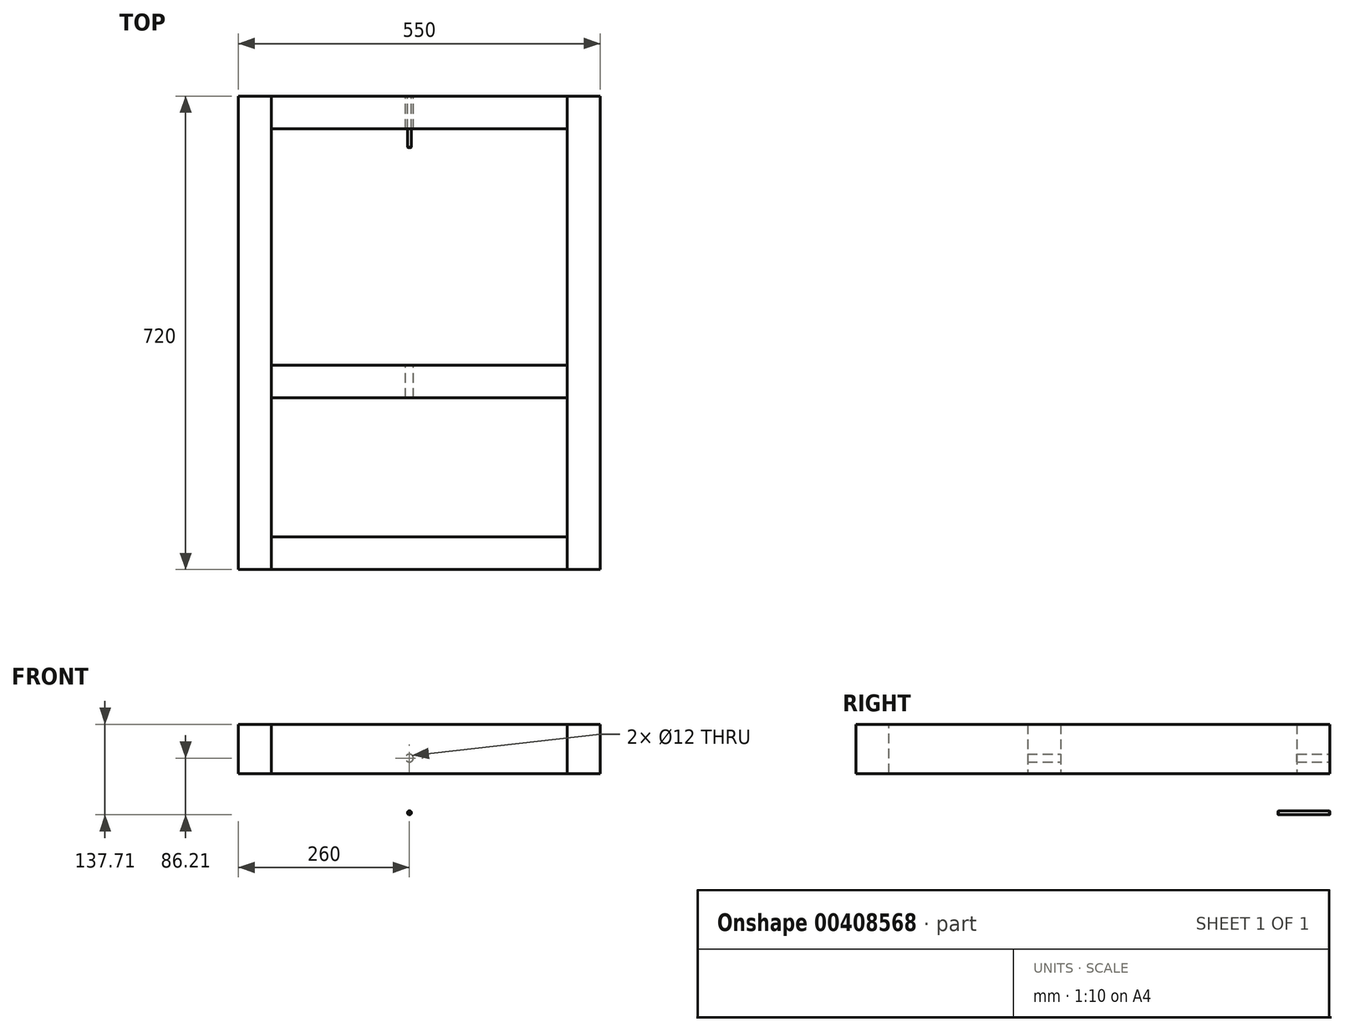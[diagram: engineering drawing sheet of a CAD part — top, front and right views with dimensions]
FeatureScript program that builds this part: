
annotation { "Feature Type Name" : "Feature", "Feature Type Description" : "" }
export const myFeature = defineFeature(function(context is Context, id is Id, definition is map)
    precondition{}
    {
        {
            var Q0;
            Q0=qCreatedBy(makeId("Front.planeOp"),FACE);
            var sketch = newSketch(context, id + "F0", { "sketchPlane" : qUnion([Q0])});
            skLineSegment(sketch, "E0.bottom", {"start": v(225, 37.5) * mm, "end": v(-225, 37.5) * mm});
            skLineSegment(sketch, "E0.top", {"start": v(225, -37.5) * mm, "end": v(-225, -37.5) * mm});
            skLineSegment(sketch, "E0.left", {"start": v(225, 37.5) * mm, "end": v(225, -37.5) * mm});
            skLineSegment(sketch, "E0.right", {"start": v(-225, 37.5) * mm, "end": v(-225, -37.5) * mm});
            skPoint(sketch, "E0.middle", {"position": v(0, 0) * mm});
            skLineSegment(sketch, "E1.bottom", {"start": v(225, 37.5) * mm, "end": v(275, 37.5) * mm});
            skLineSegment(sketch, "E1.top", {"start": v(225, -37.5) * mm, "end": v(275, -37.5) * mm});
            skLineSegment(sketch, "E1.right", {"start": v(275, 37.5) * mm, "end": v(275, -37.5) * mm});
            skLineSegment(sketch, "E2.bottom", {"start": v(-225, 37.5) * mm, "end": v(-275, 37.5) * mm});
            skLineSegment(sketch, "E2.top", {"start": v(-225, -37.5) * mm, "end": v(-275, -37.5) * mm});
            skLineSegment(sketch, "E2.right", {"start": v(-275, 37.5) * mm, "end": v(-275, -37.5) * mm});
            skLineSegment(sketch, "E3", {"start": v(225, -14) * mm, "end": v(-225, -14) * mm, "construction": true});
            skLineSegment(sketch, "E4", {"start": v(-15, 37.5) * mm, "end": v(-15, -37.5) * mm, "construction": true});
            skCircle(sketch, "E5", {"center": v(-15, -14) * mm, "radius": 6 * mm});
            skCircle(sketch, "E6", {"center": v(-15, -97.21) * mm, "radius": 3 * mm});
            skSolve(sketch);
        }
        {
            var Q0;
            Q0=makeQuery(id+"F0.imprint","IMPRINT",FACE,{"disambiguationData":[TD([[makeQuery(id+"F0.imprint","IMPRINT",EDGE,{"derivedFrom":sQuery(id+"F0.wireOp",EDGE,"E0.bottom")}),1.0]])]});
            extrude(context, id + "F1", {"entities" : qUnion([Q0]), "depth" : 50 * mm});
        }
        {
            var Q0;
            Q0=makeQuery(id+"F0.imprint","IMPRINT",FACE,{"disambiguationData":[TD([[makeQuery(id+"F0.imprint","IMPRINT",EDGE,{"derivedFrom":sQuery(id+"F0.wireOp",EDGE,"E1.bottom")}),-1.0]])]});
            extrude(context, id + "F2", {"entities" : qUnion([Q0]), "depth" : 720 * mm});
        }
        {
            var Q0;
            Q0=makeQuery(id+"F0.imprint","IMPRINT",FACE,{"disambiguationData":[TD([[makeQuery(id+"F0.imprint","IMPRINT",EDGE,{"derivedFrom":sQuery(id+"F0.wireOp",EDGE,"E2.bottom")}),1.0]])]});
            extrude(context, id + "F3", {"entities" : qUnion([Q0]), "depth" : 720 * mm});
        }
        {
            var Q0;
            Q0=makeQuery(id+"F1.opExtrude","CAP_FACE",FACE,{"disambiguationData":[OSD([sQuery(id+"F0.wireOp",EDGE,"E0.bottom"),sQuery(id+"F0.wireOp",EDGE,"E0.top"),sQuery(id+"F0.wireOp",EDGE,"E0.left"),sQuery(id+"F0.wireOp",EDGE,"E0.right"),sQuery(id+"F0.wireOp",EDGE,"E5")])],"isStart":true});
            cPlane(context, id + "F4", {"entities" : qUnion([Q0]), "cplaneType" : CPlaneType.OFFSET, "offset" : 409 * mm, "oppositeDirection" : true, "width" : 150 * mm, "height" : 150 * mm});
        }
        {
            var Q0;
            Q0=qCreatedBy(id+"F4.planeOp",FACE);
            var sketch = newSketch(context, id + "F5", { "sketchPlane" : qUnion([Q0])});
            skLineSegment(sketch, "E7.0.0", {"start": v(-225, -37.5) * mm, "end": v(225, -37.5) * mm});
            skLineSegment(sketch, "E7.0.1", {"start": v(225, -37.5) * mm, "end": v(225, 37.5) * mm});
            skLineSegment(sketch, "E7.0.2", {"start": v(225, 37.5) * mm, "end": v(-225, 37.5) * mm});
            skLineSegment(sketch, "E7.0.3", {"start": v(-225, 37.5) * mm, "end": v(-225, -37.5) * mm});
            skPoint(sketch, "E8.0", {"position": v(0, 0) * mm});
            skCircle(sketch, "E9.0", {"center": v(15, -14) * mm, "radius": 6 * mm});
            skLineSegment(sketch, "E10.0", {"start": v(-225, 37.5) * mm, "end": v(225, 37.5) * mm});
            skSolve(sketch);
        }
        {
            var Q0;
            Q0=makeQuery(id+"F5.imprint","IMPRINT",FACE,{"disambiguationData":[TD([[makeQuery(id+"F5.imprint","IMPRINT",EDGE,{"derivedFrom":sQuery(id+"F5.wireOp",EDGE,"E7.0.0")}),1.0]])]});
            extrude(context, id + "F6", {"entities" : qUnion([Q0]), "oppositeDirection" : true, "depth" : 50 * mm});
        }
        {
            var Q0;
            Q0=qCreatedBy(id+"F4.planeOp",FACE);
            cPlane(context, id + "F7", {"entities" : qUnion([Q0]), "cplaneType" : CPlaneType.OFFSET, "offset" : 311 * mm, "oppositeDirection" : true, "width" : 150 * mm, "height" : 150 * mm});
        }
        {
            var Q0;
            Q0=qCreatedBy(id+"F7.planeOp",FACE);
            var sketch = newSketch(context, id + "F8", { "sketchPlane" : qUnion([Q0])});
            skLineSegment(sketch, "E11.0", {"start": v(-225, 37.5) * mm, "end": v(225, 37.5) * mm});
            skLineSegment(sketch, "E12.0.0", {"start": v(-225, -37.5) * mm, "end": v(225, -37.5) * mm});
            skLineSegment(sketch, "E12.0.1", {"start": v(225, -37.5) * mm, "end": v(225, 37.5) * mm});
            skLineSegment(sketch, "E12.0.2", {"start": v(225, 37.5) * mm, "end": v(-225, 37.5) * mm});
            skLineSegment(sketch, "E12.0.3", {"start": v(-225, 37.5) * mm, "end": v(-225, -37.5) * mm});
            skSolve(sketch);
        }
        {
            var Q0;
            Q0=makeQuery(id+"F8.imprint","IMPRINT",FACE,{"disambiguationData":[TD([[makeQuery(id+"F8.imprint","IMPRINT",EDGE,{"derivedFrom":sQuery(id+"F8.wireOp",EDGE,"E12.0.0")}),1.0]])]});
            extrude(context, id + "F9", {"entities" : qUnion([Q0]), "depth" : 50 * mm});
        }
        {
            var Q0;
            Q0 = qSketchRegion(id + "F0", true);
            extrude(context, id + "F10", {"entities" : qUnion([Q0]), "depth" : 78.5 * mm});
        }
        {
            var Q0;
            Q0=makeQuery(id+"F10.opExtrude","CAP_EDGE",EDGE,{"disambiguationData":[OSD([sQuery(id+"F0.wireOp",EDGE,"E6")])],"isStart":true});
            var Q1;
            Q1=makeQuery(id+"F10.opExtrude","CAP_EDGE",EDGE,{"disambiguationData":[OSD([sQuery(id+"F0.wireOp",EDGE,"E6")])],"isStart":false});
            chamfer(context, id + "F11", {"entities" : qUnion([Q0, Q1]), "width" : .5 * mm, "tangentPropagation" : true});
        }
        {
            var Q0;
            Q0=makeQuery(id+"F2.opExtrude","SWEPT_BODY",BODY,{"disambiguationData":[OSD([sQuery(id+"F0.wireOp",EDGE,"E1.bottom"),sQuery(id+"F0.wireOp",EDGE,"E1.top"),sQuery(id+"F0.wireOp",EDGE,"E0.left"),sQuery(id+"F0.wireOp",EDGE,"E1.right")])]});
            var Q1;
            Q1=makeQuery(id+"F10.opExtrude","SWEPT_BODY",BODY,{"disambiguationData":[OSD([sQuery(id+"F0.wireOp",EDGE,"E0.bottom"),sQuery(id+"F0.wireOp",EDGE,"E0.top"),sQuery(id+"F0.wireOp",EDGE,"E1.bottom"),sQuery(id+"F0.wireOp",EDGE,"E1.top"),sQuery(id+"F0.wireOp",EDGE,"E1.right"),sQuery(id+"F0.wireOp",EDGE,"E2.bottom"),sQuery(id+"F0.wireOp",EDGE,"E2.top"),sQuery(id+"F0.wireOp",EDGE,"E2.right"),sQuery(id+"F0.wireOp",EDGE,"E5")])]});
            deleteBodies(context, id + "F12", {"entities" : qUnion([Q0, Q1])});
        }
        {
            var Q0;
            Q0=makeQuery(id+"F0.imprint","IMPRINT",FACE,{"disambiguationData":[TD([[makeQuery(id+"F0.imprint","IMPRINT",EDGE,{"derivedFrom":sQuery(id+"F0.wireOp",EDGE,"E1.bottom")}),-1.0]])]});
            extrude(context, id + "F13", {"entities" : qUnion([Q0]), "depth" : 720 * mm});
        }
        {
            var Q0;
            Q0=makeQuery(id+"F13.opExtrude","SWEPT_BODY",BODY,{"disambiguationData":[OSD([sQuery(id+"F0.wireOp",EDGE,"E1.bottom"),sQuery(id+"F0.wireOp",EDGE,"E1.top"),sQuery(id+"F0.wireOp",EDGE,"E0.left"),sQuery(id+"F0.wireOp",EDGE,"E1.right")])]});
            deleteBodies(context, id + "F14", {"entities" : qUnion([Q0])});
        }
        {
            var Q0;
            Q0=makeQuery(id+"F0.imprint","IMPRINT",FACE,{"disambiguationData":[TD([[makeQuery(id+"F0.imprint","IMPRINT",EDGE,{"derivedFrom":sQuery(id+"F0.wireOp",EDGE,"E1.bottom")}),-1.0]])]});
            extrude(context, id + "F15", {"entities" : qUnion([Q0]), "depth" : 720 * mm});
        }
    });
